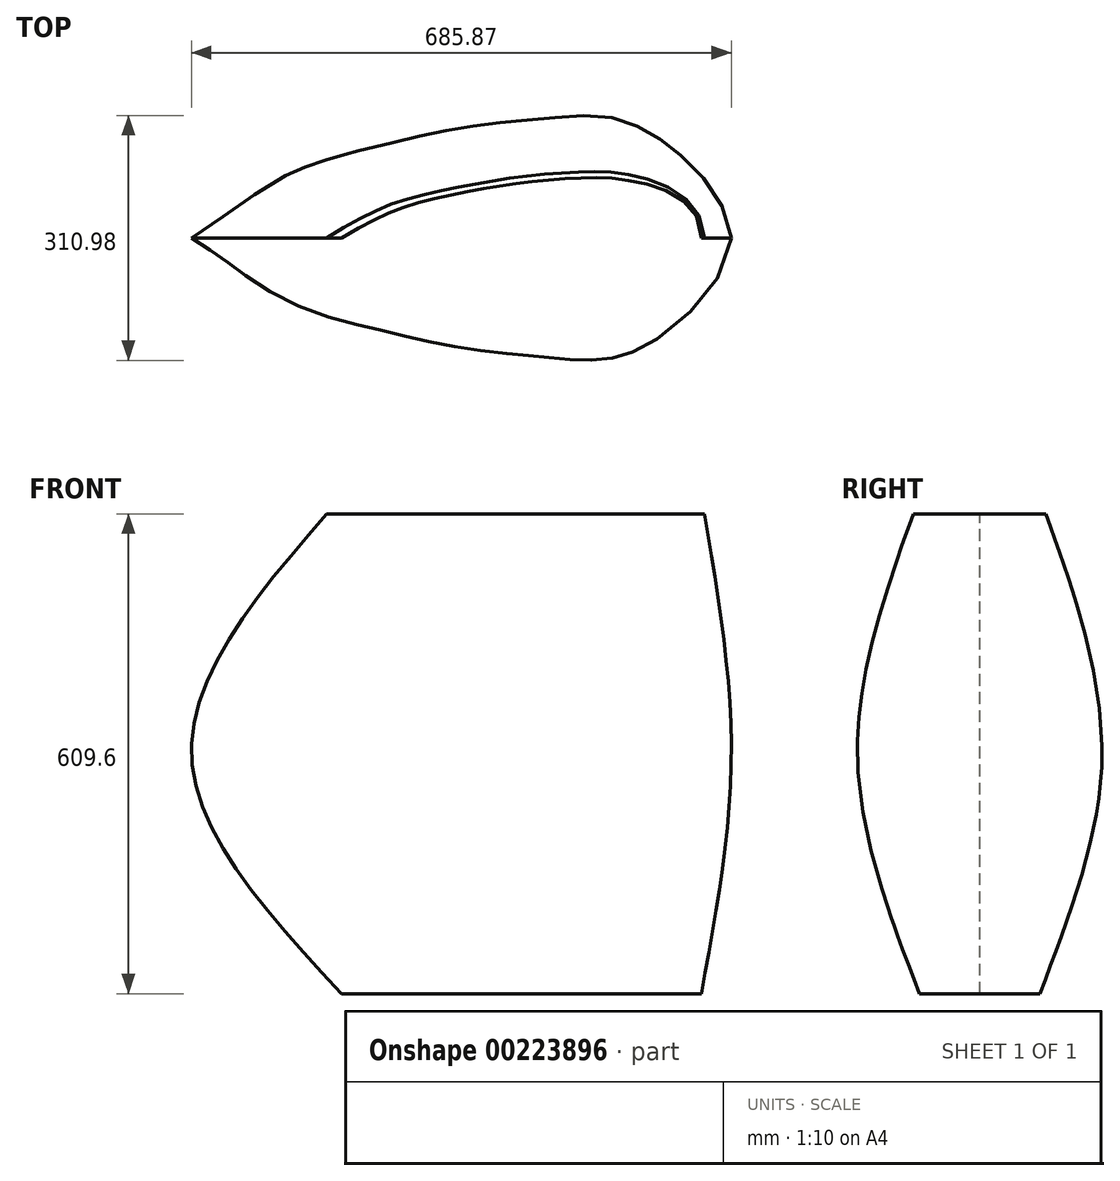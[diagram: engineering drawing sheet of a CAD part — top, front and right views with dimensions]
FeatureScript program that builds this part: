
annotation { "Feature Type Name" : "Feature", "Feature Type Description" : "" }
export const myFeature = defineFeature(function(context is Context, id is Id, definition is map)
    precondition{}
    {
        {
            var Q0;
            Q0=qCreatedBy(makeId("Top.planeOp"),FACE);
            cPlane(context, id + "F0", {"entities" : qUnion([Q0]), "cplaneType" : CPlaneType.OFFSET, "offset" : 304.8 * mm, "width" : 152.4 * mm, "height" : 152.4 * mm});
        }
        {
            var Q0;
            Q0=qCreatedBy(id+"F0.planeOp",FACE);
            cPlane(context, id + "F1", {"entities" : qUnion([Q0]), "cplaneType" : CPlaneType.OFFSET, "offset" : 304.8 * mm, "width" : 152.4 * mm, "height" : 152.4 * mm});
        }
        {
            var Q0;
            Q0=qCreatedBy(makeId("Top.planeOp"),FACE);
            var sketch = newSketch(context, id + "F2", { "sketchPlane" : qUnion([Q0])});
            skLineSegment(sketch, "E0", {"start": v(-381, 0) * mm, "end": v(76.2, 0) * mm, "construction": true});
            skLineSegment(sketch, "E1", {"start": v(-228.6, 0) * mm, "end": v(-228.6, 57.15) * mm, "construction": true});
            skLineSegment(sketch, "E2", {"start": v(-152.4, 0) * mm, "end": v(-152.4, 69.85) * mm, "construction": true});
            skLineSegment(sketch, "E3", {"start": v(-76.2, 0) * mm, "end": v(-76.2, 76.2) * mm, "construction": true});
            skLineSegment(sketch, "E4", {"start": v(0, 0) * mm, "end": v(0, 69.85) * mm, "construction": true});
            skLineSegment(sketch, "E5", {"start": v(-304.8, 0) * mm, "end": v(-304.8, 38.1) * mm, "construction": true});
            skFitSpline(sketch, "E6", {"points": [v(-381, 0) * mm, v(-304.8, 38.1) * mm, v(-228.6, 57.15) * mm, v(-152.4, 69.85) * mm, v(-76.2, 76.2) * mm, v(0, 69.85) * mm, v(76.2, 0) * mm], "startDerivative": vector(535.5, 309.18) * mm, "endDerivative": vector(0, -736.48) * mm});
            skLineSegment(sketch, "E7", {"start": v(76.2, -148.6) * mm, "end": v(76.2, 0) * mm, "construction": true});
            skLineSegment(sketch, "E8", {"start": v(-381, 0) * mm, "end": v(-301.46, 45.92) * mm, "construction": true});
            skFitSpline(sketch, "E9", {"points": [v(-381, 0) * mm, v(-304.8, -38.1) * mm, v(-228.6, -57.15) * mm, v(-152.4, -69.85) * mm, v(-76.2, -76.2) * mm, v(0, -69.85) * mm, v(76.2, 0) * mm], "startDerivative": vector(535.5, -309.18) * mm, "endDerivative": vector(0, 736.48) * mm});
            skSolve(sketch);
        }
        {
            var Q0;
            Q0=qCreatedBy(id+"F0.planeOp",FACE);
            var sketch = newSketch(context, id + "F3", { "sketchPlane" : qUnion([Q0])});
            skLineSegment(sketch, "E10", {"start": v(-571.5, 0) * mm, "end": v(114.3, 0) * mm, "construction": true});
            skLineSegment(sketch, "E11", {"start": v(-342.9, 0) * mm, "end": v(-342.9, 114.3) * mm, "construction": true});
            skLineSegment(sketch, "E12", {"start": v(-228.6, 0) * mm, "end": v(-228.6, 139.7) * mm, "construction": true});
            skLineSegment(sketch, "E13", {"start": v(-114.3, 0) * mm, "end": v(-114.3, 152.4) * mm, "construction": true});
            skLineSegment(sketch, "E14", {"start": v(0, 0) * mm, "end": v(0, 139.7) * mm, "construction": true});
            skLineSegment(sketch, "E15", {"start": v(-457.2, 0) * mm, "end": v(-457.2, 76.2) * mm, "construction": true});
            skFitSpline(sketch, "E16", {"points": [v(-571.5, 0) * mm, v(-457.2, 76.2) * mm, v(-342.9, 114.3) * mm, v(-228.6, 139.7) * mm, v(-114.3, 152.4) * mm, v(0, 139.7) * mm, v(114.3, 0) * mm], "startDerivative": vector(537.1, 310.1) * mm, "endDerivative": vector(0, -736.4) * mm});
            skLineSegment(sketch, "E17", {"start": v(114.3, 0) * mm, "end": v(114.3, 47.74) * mm, "construction": true});
            skLineSegment(sketch, "E18", {"start": v(-571.5, 0) * mm, "end": v(-240.47, 191.12) * mm, "construction": true});
            skFitSpline(sketch, "E19", {"points": [v(-571.5, 0) * mm, v(-457.2, -76.2) * mm, v(-342.9, -114.3) * mm, v(-228.6, -139.7) * mm, v(-114.3, -152.4) * mm, v(0, -139.7) * mm, v(114.3, 0) * mm], "startDerivative": vector(537.1, -310.1) * mm, "endDerivative": vector(0, 736.4) * mm});
            skSolve(sketch);
        }
        {
            var Q0;
            Q0=qCreatedBy(id+"F1.planeOp",FACE);
            var sketch = newSketch(context, id + "F4", { "sketchPlane" : qUnion([Q0])});
            skLineSegment(sketch, "E20", {"start": v(-400.05, 0) * mm, "end": v(80.01, 0) * mm, "construction": true});
            skLineSegment(sketch, "E21", {"start": v(-240.03, 0) * mm, "end": v(-240.03, 62.87) * mm, "construction": true});
            skLineSegment(sketch, "E22", {"start": v(-160.02, 0) * mm, "end": v(-160.02, 76.84) * mm, "construction": true});
            skLineSegment(sketch, "E23", {"start": v(-80.01, 0) * mm, "end": v(-80.01, 83.82) * mm, "construction": true});
            skLineSegment(sketch, "E24", {"start": v(0, 0) * mm, "end": v(0, 76.84) * mm, "construction": true});
            skLineSegment(sketch, "E25", {"start": v(-320.04, 0) * mm, "end": v(-320.04, 41.91) * mm, "construction": true});
            skFitSpline(sketch, "E26", {"points": [v(-400.05, 0) * mm, v(-320.04, 41.91) * mm, v(-240.03, 62.87) * mm, v(-160.02, 76.84) * mm, v(-80.01, 83.82) * mm, v(0, 76.84) * mm, v(80.01, 0) * mm], "startDerivative": vector(535.5, 309.18) * mm, "endDerivative": vector(0, -736.48) * mm});
            skLineSegment(sketch, "E27", {"start": v(80.01, 0) * mm, "end": v(80.01, 47.74) * mm, "construction": true});
            skLineSegment(sketch, "E28", {"start": v(-400.05, 0) * mm, "end": v(-197.61, 116.88) * mm, "construction": true});
            skFitSpline(sketch, "E29", {"points": [v(-400.05, 0) * mm, v(-320.04, -41.91) * mm, v(-240.03, -62.87) * mm, v(-160.02, -76.84) * mm, v(-80.01, -83.82) * mm, v(0, -76.84) * mm, v(80.01, 0) * mm], "startDerivative": vector(535.5, -309.18) * mm, "endDerivative": vector(0, 736.48) * mm});
            skSolve(sketch);
        }
        {
            var Q0;
            Q0 = qSketchRegion(id + "F2", true);
            var Q1;
            Q1 = qSketchRegion(id + "F3", true);
            var Q2;
            Q2 = qSketchRegion(id + "F4", true);
            var Q3;
            Q3 = qConstructionFilter(qBodyType(qCreatedBy(id + "F2" ,EDGE), BodyType.WIRE), ConstructionObject.NO);
            var Q4;
            Q4 = qConstructionFilter(qBodyType(qCreatedBy(id + "F3" ,EDGE), BodyType.WIRE), ConstructionObject.NO);
            var Q5;
            Q5 = qConstructionFilter(qBodyType(qCreatedBy(id + "F4" ,EDGE), BodyType.WIRE), ConstructionObject.NO);
            loft(context, id + "F5", {"bodyType" : ToolBodyType.SURFACE, "sheetProfilesArray" : [{ "sheetProfileEntities" : qUnion([Q0]) }, { "sheetProfileEntities" : qUnion([Q1]) }, { "sheetProfileEntities" : qUnion([Q2]) }], "wireProfilesArray" : [{ "wireProfileEntities" : qUnion([Q3]) }, { "wireProfileEntities" : qUnion([Q4]) }, { "wireProfileEntities" : qUnion([Q5]) }]});
        }
    });
